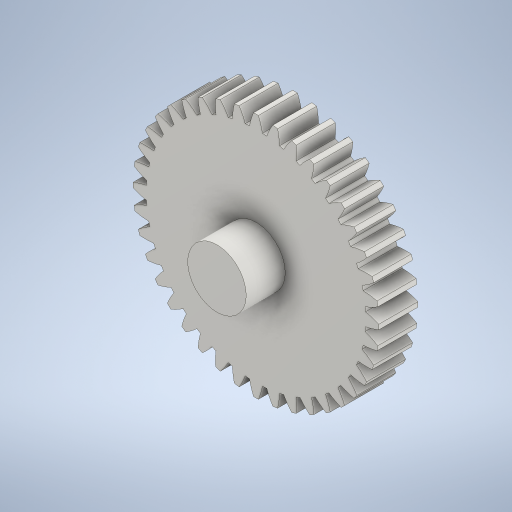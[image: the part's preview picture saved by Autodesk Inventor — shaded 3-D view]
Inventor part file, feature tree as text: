
AUTODESK INVENTOR PART (.ipt)
format: ipt  version: 2023.2 (Build 272271000, 271)  size: 458,752 bytes
history: native  units: mm (DEFAULTED — no unit token found)
features: plane x3, other x3, sketch x3, extrude x2
ambient origin geometry x8: Origin, YZ Plane, XZ Plane, XY Plane, X Axis, Y Axis, Z Axis, Center Point
bodies: Solid1 (feature_tree)
feature tree (11):
  extrude  "Extrusion1"  Depth=20.0mm TaperAngle=0.0deg
  plane  "Work Plane2"
  plane  "Work Plane8"
  plane  "Work Plane9"
  other  "Spur Gear"
  extrude  "Extrusion2"  Depth=10.0mm TaperAngle=0.0deg
  sketch  "Sketch1"  dims[d0=126.0mm d1=20.0mm d2=0.0mm]
  sketch  "Sketch2"  dims[d3=120.0mm d4=10.0mm d5=0.0mm]
  other  "Srf1"
  sketch  "Sketch3"  dims[d16=90.0mm d17=0.0mm d34=0.785398mm d39=0.0mm d41=0.0mm d43=90.0mm d46=90.0mm d47=0.0mm d48=0.0mm d49=30.0mm d50=20.0mm d51=0.0mm]
  other  "Pitch Diameter"
